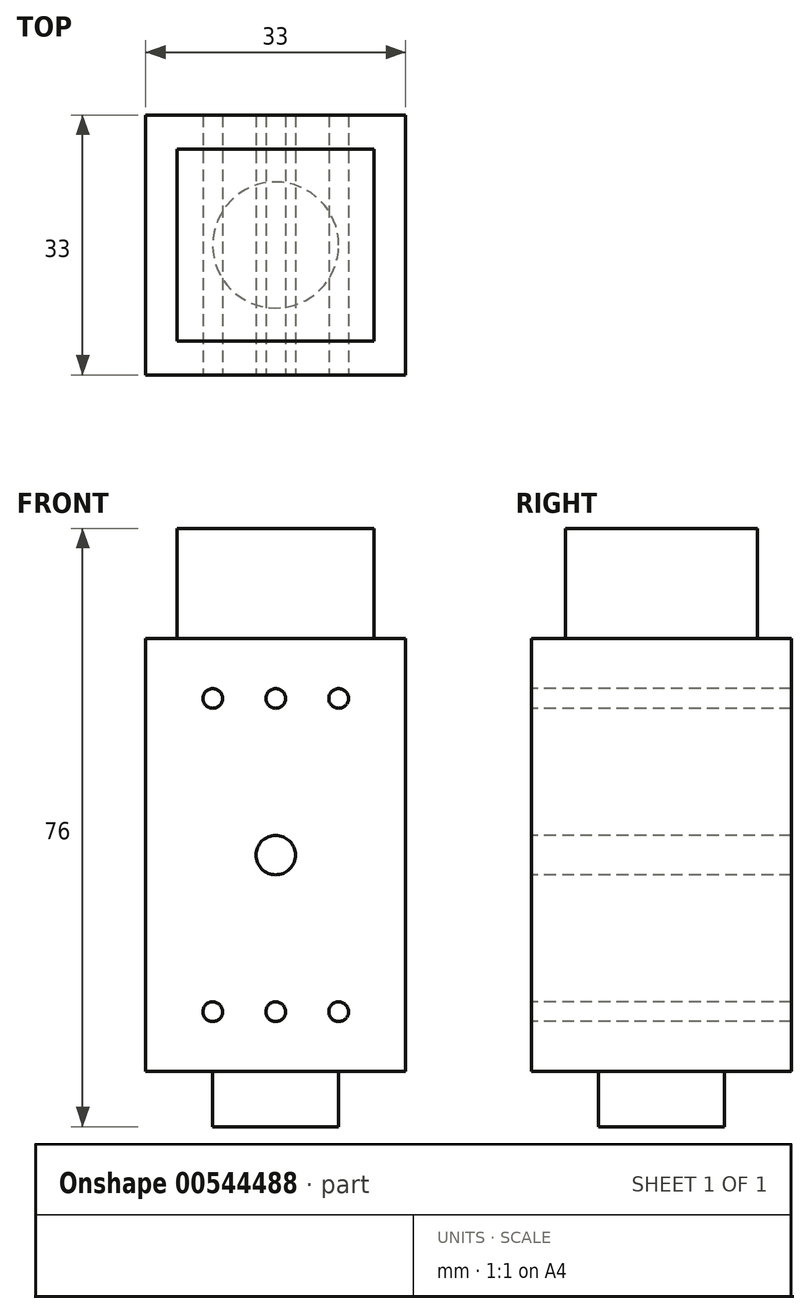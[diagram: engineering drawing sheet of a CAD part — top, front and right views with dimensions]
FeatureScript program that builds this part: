
annotation { "Feature Type Name" : "Feature", "Feature Type Description" : "" }
export const myFeature = defineFeature(function(context is Context, id is Id, definition is map)
    precondition{}
    {
        {
            var Q0;
            Q0=qCreatedBy(makeId("Top.planeOp"),FACE);
            var sketch = newSketch(context, id + "F0", { "sketchPlane" : qUnion([Q0])});
            skLineSegment(sketch, "E0.bottom", {"start": v(16.5, -16.5) * mm, "end": v(-16.5, -16.5) * mm});
            skLineSegment(sketch, "E0.top", {"start": v(16.5, 16.5) * mm, "end": v(-16.5, 16.5) * mm});
            skLineSegment(sketch, "E0.left", {"start": v(16.5, -16.5) * mm, "end": v(16.5, 16.5) * mm});
            skLineSegment(sketch, "E0.right", {"start": v(-16.5, -16.5) * mm, "end": v(-16.5, 16.5) * mm});
            skPoint(sketch, "E0.middle", {"position": v(0, 0) * mm});
            skSolve(sketch);
        }
        {
            var Q0;
            Q0 = qSketchRegion(id + "F0", true);
            extrude(context, id + "F1", {"entities" : qUnion([Q0]), "depth" : 55 * mm, "offsetDistance" : 25 * mm});
        }
        {
            var Q0;
            Q0=makeQuery(id+"F1.opExtrude","CAP_FACE",FACE,{"disambiguationData":[OSD([sQuery(id+"F0.wireOp",EDGE,"E0.bottom"),sQuery(id+"F0.wireOp",EDGE,"E0.top"),sQuery(id+"F0.wireOp",EDGE,"E0.left"),sQuery(id+"F0.wireOp",EDGE,"E0.right")])],"isStart":false});
            var sketch = newSketch(context, id + "F2", { "sketchPlane" : qUnion([Q0])});
            skLineSegment(sketch, "E1.bottom", {"start": v(12.51, -12.2) * mm, "end": v(-12.51, -12.2) * mm});
            skLineSegment(sketch, "E1.top", {"start": v(12.51, 12.2) * mm, "end": v(-12.51, 12.2) * mm});
            skLineSegment(sketch, "E1.left", {"start": v(12.51, -12.2) * mm, "end": v(12.51, 12.2) * mm});
            skLineSegment(sketch, "E1.right", {"start": v(-12.51, -12.2) * mm, "end": v(-12.51, 12.2) * mm});
            skPoint(sketch, "E1.middle", {"position": v(0, 0) * mm});
            skSolve(sketch);
        }
        {
            var Q0;
            Q0 = qSketchRegion(id + "F2", true);
            extrude(context, id + "F3", {"entities" : qUnion([Q0]), "operationType" : NewBodyOperationType.ADD, "depth" : 14 * mm, "offsetDistance" : 25 * mm});
        }
        {
            var Q0;
            Q0=makeQuery(id+"F1.opExtrude","CAP_FACE",FACE,{"disambiguationData":[OSD([sQuery(id+"F0.wireOp",EDGE,"E0.bottom"),sQuery(id+"F0.wireOp",EDGE,"E0.top"),sQuery(id+"F0.wireOp",EDGE,"E0.left"),sQuery(id+"F0.wireOp",EDGE,"E0.right")])],"isStart":true});
            var sketch = newSketch(context, id + "F4", { "sketchPlane" : qUnion([Q0])});
            skCircle(sketch, "E2", {"center": v(0, 0) * mm, "radius": 8 * mm});
            skSolve(sketch);
        }
        {
            var Q0;
            Q0 = qSketchRegion(id + "F4", true);
            extrude(context, id + "F5", {"entities" : qUnion([Q0]), "operationType" : NewBodyOperationType.ADD, "depth" : 7 * mm, "offsetDistance" : 25 * mm});
        }
        {
            var Q0;
            Q0=makeQuery(id+"F1.opExtrude","SWEPT_FACE",FACE,{"disambiguationData":[OSD([sQuery(id+"F0.wireOp",EDGE,"E0.bottom")])]});
            var sketch = newSketch(context, id + "F6", { "sketchPlane" : qUnion([Q0])});
            skLineSegment(sketch, "E3.bottom", {"start": v(-8, 47.4) * mm, "end": v(8, 47.4) * mm});
            skLineSegment(sketch, "E3.top", {"start": v(-8, 7.6) * mm, "end": v(8, 7.6) * mm});
            skLineSegment(sketch, "E3.left", {"start": v(-8, 47.4) * mm, "end": v(-8, 7.6) * mm});
            skLineSegment(sketch, "E3.right", {"start": v(8, 47.4) * mm, "end": v(8, 7.6) * mm});
            skPoint(sketch, "E3.middle", {"position": v(0, 27.5) * mm});
            skLineSegment(sketch, "E4", {"start": v(-16.5, 55) * mm, "end": v(16.5, 0) * mm, "construction": true});
            skPoint(sketch, "E5", {"position": v(0, 47.4) * mm});
            skPoint(sketch, "E6", {"position": v(0, 7.6) * mm});
            skSolve(sketch);
        }
        {
            var Q0;
            Q0=sQuery(id+"F6.wireOp",VERTEX,"E3.left.start");
            var Q1;
            Q1=sQuery(id+"F6.wireOp",VERTEX,"E5");
            var Q2;
            Q2=sQuery(id+"F6.wireOp",VERTEX,"E3.bottom.end");
            var Q3;
            Q3=sQuery(id+"F6.wireOp",VERTEX,"E3.right.end");
            var Q4;
            Q4=sQuery(id+"F6.wireOp",VERTEX,"E6");
            var Q5;
            Q5=sQuery(id+"F6.wireOp",VERTEX,"E3.left.end");
            var Q6;
            Q6=makeQuery(id+"F1.opExtrude","SWEPT_BODY",BODY,{"disambiguationData":[OSD([sQuery(id+"F0.wireOp",EDGE,"E0.bottom"),sQuery(id+"F0.wireOp",EDGE,"E0.top"),sQuery(id+"F0.wireOp",EDGE,"E0.left"),sQuery(id+"F0.wireOp",EDGE,"E0.right")])]});
            hole(context, id + "F7", {"style" : HoleStyle.SIMPLE, "endStyle" : HoleEndStyle.THROUGH, "standardTappedOrClearance" : lookupTablePath({ "standard" : "ISO", "engagement" : "75%", "pitch" : "0.5 mm", "size" : "M3", "type" : "Tapped" }), "standardBlindInLast" : lookupTablePath({ "standard" : "ISO", "engagement" : "75%", "pitch" : "0.5 mm", "size" : "M3", "type" : "Tapped" }), "holeDiameter" : 2.5 * mm, "showTappedDepth" : true, "tappedDepth" : 12 * mm, "tapClearance" : 3, "locations" : qUnion([Q0, Q1, Q2, Q3, Q4, Q5]), "scope" : qUnion([Q6]), "majorDiameter" : 3 * mm});
        }
        {
            var Q0;
            Q0=sQuery(id+"F6.wireOp",VERTEX,"E3.middle");
            var Q1;
            Q1=makeQuery(id+"F1.opExtrude","SWEPT_BODY",BODY,{"disambiguationData":[OSD([sQuery(id+"F0.wireOp",EDGE,"E0.bottom"),sQuery(id+"F0.wireOp",EDGE,"E0.top"),sQuery(id+"F0.wireOp",EDGE,"E0.left"),sQuery(id+"F0.wireOp",EDGE,"E0.right")])]});
            hole(context, id + "F8", {"style" : HoleStyle.SIMPLE, "endStyle" : HoleEndStyle.THROUGH, "standardTappedOrClearance" : lookupTablePath({ "standard" : "ISO", "engagement" : "75%", "pitch" : "1 mm", "size" : "M6", "type" : "Tapped" }), "standardBlindInLast" : lookupTablePath({ "standard" : "ISO", "engagement" : "75%", "pitch" : "1 mm", "size" : "M6", "type" : "Tapped" }), "holeDiameter" : 5 * mm, "showTappedDepth" : true, "tappedDepth" : 12 * mm, "tapClearance" : 3, "locations" : qUnion([Q0]), "scope" : qUnion([Q1]), "majorDiameter" : 6 * mm});
        }
    });
